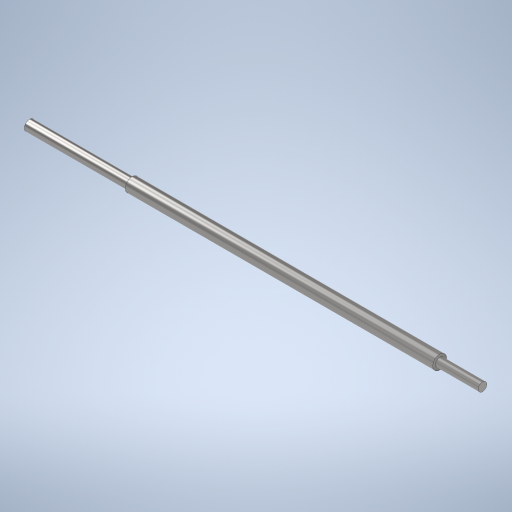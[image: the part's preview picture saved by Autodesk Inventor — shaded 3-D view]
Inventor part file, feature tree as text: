
AUTODESK INVENTOR PART (.ipt)
format: ipt  version: 2024 (Build 280153000, 153)  size: 293,376 bytes
history: native  units: in
note: dims shown in document units (in); Inventor stores cm internally (conversion verified against a paired STEP export)
features: extrude x9, sketch x9, projected_geometry x6
ambient origin geometry x8: Origin, YZ Plane, XZ Plane, XY Plane, X Axis, Y Axis, Z Axis, Center Point
bodies: Solid1 (feature_tree)
feature tree (24):
  extrude  "Extrusion1"  Depth=12.0in TaperAngle=0.0deg
  extrude  "Extrusion2"  Depth=15.1688in TaperAngle=0.0deg
  extrude  "Extrusion3"  Depth=14.5438in TaperAngle=0.0deg
  extrude  "Extrusion4"  Depth=0.9843in TaperAngle=0.0deg
  extrude  "Extrusion5"  Depth=0.9843in TaperAngle=0.0deg
  extrude  "Extrusion6"  Depth=0.9843in TaperAngle=0.0deg
  extrude  "Extrusion7"  Depth=3.937in TaperAngle=0.0deg
  extrude  "Extrusion8"  Depth=2.3622in
  extrude  "Extrusion9"  [1 undecoded]
  sketch  "Sketch1"  dims[d0=0.5in d1=12.0in d2=0.0in]
  sketch  "Sketch2"  dims[d3=0.375in d4=15.1688in d5=0.0in]
  sketch  "Sketch3"  dims[d6=0.315in d7=14.5438in d8=0.0in]
  projected_geometry  "Projected Loop1"
  sketch  "Sketch4"  dims[d9=0.2362in d10=0.9843in d11=0.0in]
  projected_geometry  "Projected Loop2"
  sketch  "Sketch5"  dims[d12=0.1969in d13=0.9843in d14=0.0in]
  projected_geometry  "Projected Loop3"
  sketch  "Sketch7"  dims[d15=0.1969in d16=0.9843in d17=0.0in]
  projected_geometry  "Projected Loop4"
  sketch  "Sketch8"  dims[d18=0.315in d19=3.937in d20=0.0in]
  sketch  "Sketch9"  dims[d21=2.3622in d22=0.0in d23=0.2362in]
  projected_geometry  "Projected Loop5"
  sketch  "Sketch10"  dims[d24=2.3622in d25=0.0in]
  projected_geometry  "Projected Loop6"
note: 1 required parameter value undecoded (feature->parameter linkage not recoverable at this tier; creation-order binding heuristic only, values carry confidence <= 0.55)
